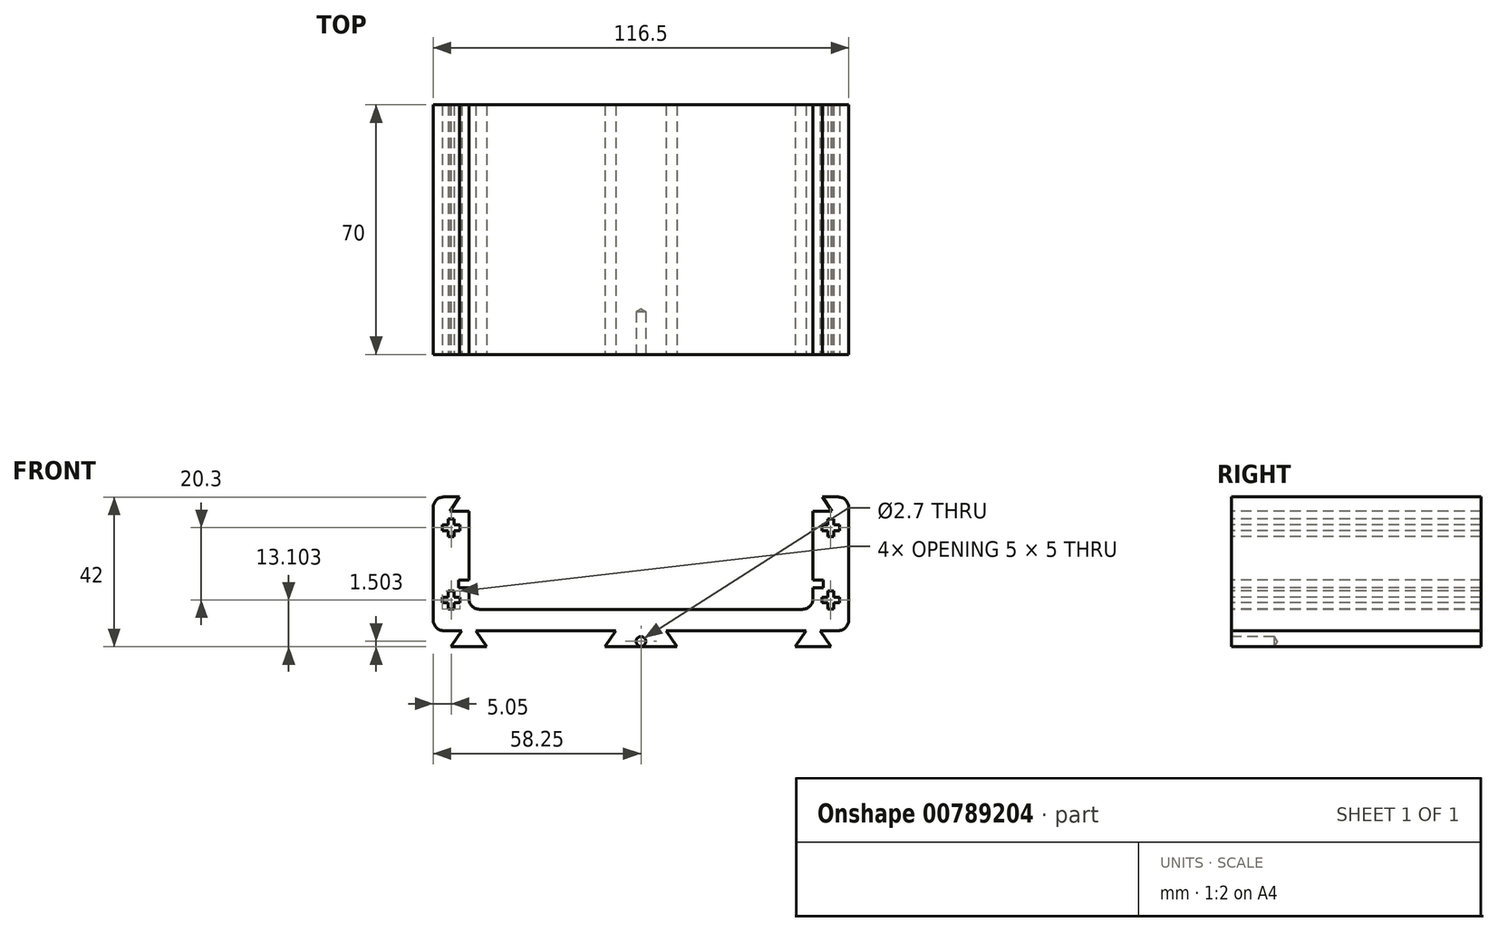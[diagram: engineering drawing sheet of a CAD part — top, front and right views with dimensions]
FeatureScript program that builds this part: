
annotation { "Feature Type Name" : "Feature", "Feature Type Description" : "" }
export const myFeature = defineFeature(function(context is Context, id is Id, definition is map)
    precondition{}
    {
        {
            var Q0;
            Q0=qCreatedBy(makeId("Front.planeOp"),FACE);
            var sketch = newSketch(context, id + "F0", { "sketchPlane" : qUnion([Q0])});
            skLineSegment(sketch, "E0", {"start": v(0, -17) * mm, "end": v(-10.04, -17) * mm});
            skLineSegment(sketch, "E1", {"start": v(-10.04, -17) * mm, "end": v(-7, -12.5) * mm});
            skLineSegment(sketch, "E2", {"start": v(-7, -12.5) * mm, "end": v(-46.25, -12.5) * mm});
            skLineSegment(sketch, "E3", {"start": v(-46.25, -12.5) * mm, "end": v(-43.21, -17) * mm});
            skLineSegment(sketch, "E4", {"start": v(-43.21, -17) * mm, "end": v(-53.29, -17) * mm});
            skLineSegment(sketch, "E5", {"start": v(-53.29, -17) * mm, "end": v(-50.25, -12.5) * mm});
            skLineSegment(sketch, "E6", {"start": v(-50.25, -12.5) * mm, "end": v(-55.25, -12.5) * mm});
            skLineSegment(sketch, "E7", {"start": v(-58.25, -9.5) * mm, "end": v(-58.25, 22) * mm});
            skLineSegment(sketch, "E8", {"start": v(-55.25, 25) * mm, "end": v(-50.87, 25) * mm});
            skLineSegment(sketch, "E9", {"start": v(-50.87, 25) * mm, "end": v(-53.5, 21) * mm});
            skLineSegment(sketch, "E10", {"start": v(-53.5, 21) * mm, "end": v(-48.25, 21) * mm});
            skLineSegment(sketch, "E11", {"start": v(-48.25, 21) * mm, "end": v(-48.25, 1.7) * mm});
            skLineSegment(sketch, "E12", {"start": v(-48.25, 1.7) * mm, "end": v(-51.1, 1.7) * mm});
            skLineSegment(sketch, "E13", {"start": v(-51.1, 1.7) * mm, "end": v(-51.1, -0.5) * mm});
            skLineSegment(sketch, "E14", {"start": v(-51.1, -0.5) * mm, "end": v(-48.25, -0.5) * mm});
            skLineSegment(sketch, "E15", {"start": v(-48.25, -0.5) * mm, "end": v(-48.25, -3.5) * mm});
            skLineSegment(sketch, "E16", {"start": v(-45.25, -6.5) * mm, "end": v(0, -6.5) * mm});
            skLineSegment(sketch, "E17", {"start": v(-48.25, 29.47) * mm, "end": v(-48.25, -26.87) * mm, "construction": true});
            skPoint(sketch, "E18.visualSharp", {"position": v(-58.25, 25) * mm});
            skArc(sketch, "E18.filletArc", {"start": v(-55.25, 25) * mm, "mid": v(-57.37, 24.11) * mm, "end": v(-58.25, 22) * mm});
            skPoint(sketch, "E19.visualSharp", {"position": v(-58.25, -12.5) * mm});
            skArc(sketch, "E19.filletArc", {"start": v(-58.25, -9.5) * mm, "mid": v(-57.37, -11.63) * mm, "end": v(-55.25, -12.5) * mm});
            skPoint(sketch, "E20.visualSharp", {"position": v(-48.25, -6.5) * mm});
            skArc(sketch, "E20.filletArc", {"start": v(-48.25, -3.5) * mm, "mid": v(-47.37, -5.63) * mm, "end": v(-45.25, -6.5) * mm});
            skLineSegment(sketch, "E21", {"start": v(-53.2, 35.2) * mm, "end": v(-53.2, -9.28) * mm, "construction": true});
            skLineSegment(sketch, "E22", {"start": v(-92.18, 6.24) * mm, "end": v(0, 6.24) * mm, "construction": true});
            skArc(sketch, "E23.MirrorCS", {"start": v(48.25, -3.5) * mm, "mid": v(47.37, -5.63) * mm, "end": v(45.25, -6.5) * mm});
            skArc(sketch, "E24.MirrorCS", {"start": v(55.25, 25) * mm, "mid": v(57.37, 24.11) * mm, "end": v(58.25, 22) * mm});
            skLineSegment(sketch, "E25.MirrorCS", {"start": v(48.25, -0.5) * mm, "end": v(48.25, -3.5) * mm});
            skLineSegment(sketch, "E26.MirrorCS", {"start": v(46.25, -12.5) * mm, "end": v(43.21, -17) * mm});
            skLineSegment(sketch, "E27.MirrorCS", {"start": v(51.1, 1.7) * mm, "end": v(51.1, -0.5) * mm});
            skLineSegment(sketch, "E28.MirrorCS", {"start": v(53.29, -17) * mm, "end": v(50.25, -12.5) * mm});
            skLineSegment(sketch, "E29.MirrorCS", {"start": v(10.04, -17) * mm, "end": v(7, -12.5) * mm});
            skLineSegment(sketch, "E30.MirrorCS", {"start": v(48.25, 1.7) * mm, "end": v(51.1, 1.7) * mm});
            skLineSegment(sketch, "E31.MirrorCS", {"start": v(51.1, -0.5) * mm, "end": v(48.25, -0.5) * mm});
            skArc(sketch, "E32.MirrorCS", {"start": v(58.25, -9.5) * mm, "mid": v(57.37, -11.63) * mm, "end": v(55.25, -12.5) * mm});
            skLineSegment(sketch, "E33.MirrorCS", {"start": v(45.25, -6.5) * mm, "end": v(0, -6.5) * mm});
            skLineSegment(sketch, "E34.MirrorCS", {"start": v(48.25, 29.47) * mm, "end": v(48.25, -26.87) * mm, "construction": true});
            skLineSegment(sketch, "E35.MirrorCS", {"start": v(0, -17) * mm, "end": v(10.04, -17) * mm});
            skPoint(sketch, "E36.MirrorP", {"position": v(58.25, -12.5) * mm});
            skLineSegment(sketch, "E37.MirrorCS", {"start": v(7, -12.5) * mm, "end": v(46.25, -12.5) * mm});
            skLineSegment(sketch, "E38.MirrorCS", {"start": v(43.21, -17) * mm, "end": v(53.29, -17) * mm});
            skPoint(sketch, "E39.MirrorP", {"position": v(58.25, 25) * mm});
            skLineSegment(sketch, "E40.MirrorCS", {"start": v(50.25, -12.5) * mm, "end": v(55.25, -12.5) * mm});
            skLineSegment(sketch, "E41.MirrorCS", {"start": v(53.2, 35.2) * mm, "end": v(53.2, -9.28) * mm, "construction": true});
            skPoint(sketch, "E42.MirrorP", {"position": v(48.25, -6.5) * mm});
            skLineSegment(sketch, "E43.MirrorCS", {"start": v(58.25, -9.5) * mm, "end": v(58.25, 22) * mm});
            skLineSegment(sketch, "E44.MirrorCS", {"start": v(53.5, 21) * mm, "end": v(48.25, 21) * mm});
            skLineSegment(sketch, "E45.MirrorCS", {"start": v(48.25, 21) * mm, "end": v(48.25, 1.7) * mm});
            skLineSegment(sketch, "E46.MirrorCS", {"start": v(55.25, 25) * mm, "end": v(50.87, 25) * mm});
            skLineSegment(sketch, "E47.MirrorCS", {"start": v(50.87, 25) * mm, "end": v(53.5, 21) * mm});
            skPoint(sketch, "E48", {"position": v(-53.2, 16.4) * mm});
            skPoint(sketch, "E49", {"position": v(-53.2, -3.9) * mm});
            skLineSegment(sketch, "E50", {"start": v(-55.7, 17.2) * mm, "end": v(-54, 17.2) * mm});
            skLineSegment(sketch, "E51", {"start": v(-54, 17.2) * mm, "end": v(-54, 18.9) * mm});
            skLineSegment(sketch, "E52", {"start": v(-54, 18.9) * mm, "end": v(-52.4, 18.9) * mm});
            skLineSegment(sketch, "E53", {"start": v(-52.4, 18.9) * mm, "end": v(-52.4, 17.2) * mm});
            skLineSegment(sketch, "E54", {"start": v(-52.4, 17.2) * mm, "end": v(-50.7, 17.2) * mm});
            skLineSegment(sketch, "E55", {"start": v(-50.7, 17.2) * mm, "end": v(-50.7, 15.6) * mm});
            skLineSegment(sketch, "E56", {"start": v(-50.7, 15.6) * mm, "end": v(-52.4, 15.6) * mm});
            skLineSegment(sketch, "E57", {"start": v(-52.4, 15.6) * mm, "end": v(-52.4, 13.9) * mm});
            skLineSegment(sketch, "E58", {"start": v(-52.4, 13.9) * mm, "end": v(-54, 13.9) * mm});
            skLineSegment(sketch, "E59", {"start": v(-54, 13.9) * mm, "end": v(-54, 15.6) * mm});
            skLineSegment(sketch, "E60", {"start": v(-54, 15.6) * mm, "end": v(-55.7, 15.6) * mm});
            skLineSegment(sketch, "E61", {"start": v(-55.7, 15.6) * mm, "end": v(-55.7, 17.2) * mm});
            skLineSegment(sketch, "E62", {"start": v(-50.4, 16.4) * mm, "end": v(-59.4, 16.4) * mm, "construction": true});
            skLineSegment(sketch, "E63", {"start": v(-49.34, -3.9) * mm, "end": v(-57.36, -3.9) * mm, "construction": true});
            skLineSegment(sketch, "E64", {"start": v(-54, -1.4) * mm, "end": v(-52.4, -1.4) * mm});
            skLineSegment(sketch, "E65", {"start": v(-52.4, -1.4) * mm, "end": v(-52.4, -3.1) * mm});
            skLineSegment(sketch, "E66", {"start": v(-52.4, -3.1) * mm, "end": v(-50.7, -3.1) * mm});
            skLineSegment(sketch, "E67", {"start": v(-50.7, -3.1) * mm, "end": v(-50.7, -4.7) * mm});
            skLineSegment(sketch, "E68", {"start": v(-50.7, -4.7) * mm, "end": v(-52.4, -4.7) * mm});
            skLineSegment(sketch, "E69", {"start": v(-52.4, -4.7) * mm, "end": v(-52.4, -6.4) * mm});
            skLineSegment(sketch, "E70", {"start": v(-52.4, -6.4) * mm, "end": v(-54, -6.4) * mm});
            skLineSegment(sketch, "E71", {"start": v(-54, -6.4) * mm, "end": v(-54, -4.7) * mm});
            skLineSegment(sketch, "E72", {"start": v(-54, -4.7) * mm, "end": v(-55.7, -4.7) * mm});
            skLineSegment(sketch, "E73", {"start": v(-55.7, -4.7) * mm, "end": v(-55.7, -3.1) * mm});
            skLineSegment(sketch, "E74", {"start": v(-55.7, -3.1) * mm, "end": v(-54, -3.1) * mm});
            skLineSegment(sketch, "E75", {"start": v(-54, -3.1) * mm, "end": v(-54, -1.4) * mm});
            skLineSegment(sketch, "E76.MirrorCS", {"start": v(54, 17.2) * mm, "end": v(54, 18.9) * mm});
            skLineSegment(sketch, "E77.MirrorCS", {"start": v(54, 18.9) * mm, "end": v(52.4, 18.9) * mm});
            skLineSegment(sketch, "E78.MirrorCS", {"start": v(52.4, 18.9) * mm, "end": v(52.4, 17.2) * mm});
            skLineSegment(sketch, "E79.MirrorCS", {"start": v(52.4, 17.2) * mm, "end": v(50.7, 17.2) * mm});
            skLineSegment(sketch, "E80.MirrorCS", {"start": v(50.7, 17.2) * mm, "end": v(50.7, 15.6) * mm});
            skLineSegment(sketch, "E81.MirrorCS", {"start": v(50.7, 15.6) * mm, "end": v(52.4, 15.6) * mm});
            skLineSegment(sketch, "E82.MirrorCS", {"start": v(52.4, 15.6) * mm, "end": v(52.4, 13.9) * mm});
            skLineSegment(sketch, "E83.MirrorCS", {"start": v(52.4, 13.9) * mm, "end": v(54, 13.9) * mm});
            skLineSegment(sketch, "E84.MirrorCS", {"start": v(54, 13.9) * mm, "end": v(54, 15.6) * mm});
            skLineSegment(sketch, "E85.MirrorCS", {"start": v(54, 15.6) * mm, "end": v(55.7, 15.6) * mm});
            skLineSegment(sketch, "E86.MirrorCS", {"start": v(55.7, 15.6) * mm, "end": v(55.7, 17.2) * mm});
            skLineSegment(sketch, "E87.MirrorCS", {"start": v(55.7, 17.2) * mm, "end": v(54, 17.2) * mm});
            skLineSegment(sketch, "E88.MirrorCS", {"start": v(54, -1.4) * mm, "end": v(52.4, -1.4) * mm});
            skLineSegment(sketch, "E89.MirrorCS", {"start": v(52.4, -1.4) * mm, "end": v(52.4, -3.1) * mm});
            skLineSegment(sketch, "E90.MirrorCS", {"start": v(52.4, -3.1) * mm, "end": v(50.7, -3.1) * mm});
            skLineSegment(sketch, "E91.MirrorCS", {"start": v(50.7, -3.1) * mm, "end": v(50.7, -4.7) * mm});
            skLineSegment(sketch, "E92.MirrorCS", {"start": v(50.7, -4.7) * mm, "end": v(52.4, -4.7) * mm});
            skLineSegment(sketch, "E93.MirrorCS", {"start": v(52.4, -4.7) * mm, "end": v(52.4, -6.4) * mm});
            skLineSegment(sketch, "E94.MirrorCS", {"start": v(52.4, -6.4) * mm, "end": v(54, -6.4) * mm});
            skLineSegment(sketch, "E95.MirrorCS", {"start": v(54, -6.4) * mm, "end": v(54, -4.7) * mm});
            skLineSegment(sketch, "E96.MirrorCS", {"start": v(54, -4.7) * mm, "end": v(55.7, -4.7) * mm});
            skLineSegment(sketch, "E97.MirrorCS", {"start": v(55.7, -4.7) * mm, "end": v(55.7, -3.1) * mm});
            skLineSegment(sketch, "E98.MirrorCS", {"start": v(55.7, -3.1) * mm, "end": v(54, -3.1) * mm});
            skLineSegment(sketch, "E99.MirrorCS", {"start": v(54, -3.1) * mm, "end": v(54, -1.4) * mm});
            skSolve(sketch);
        }
        {
            var Q0;
            Q0=qSketchRegion(id+"F0",true);
            extrude(context, id + "F1", {"entities" : qUnion([Q0]), "oppositeDirection" : true, "depth" : 70 * mm});
        }
        {
            var Q0;
            Q0=makeQuery(id+"F1.opExtrude","CAP_FACE",FACE,{"disambiguationData":[OSD([sQuery(id+"F0.wireOp",EDGE,"E0"),sQuery(id+"F0.wireOp",EDGE,"E1"),sQuery(id+"F0.wireOp",EDGE,"E2"),sQuery(id+"F0.wireOp",EDGE,"E3"),sQuery(id+"F0.wireOp",EDGE,"E4"),sQuery(id+"F0.wireOp",EDGE,"E5"),sQuery(id+"F0.wireOp",EDGE,"E6"),sQuery(id+"F0.wireOp",EDGE,"E7"),sQuery(id+"F0.wireOp",EDGE,"E8"),sQuery(id+"F0.wireOp",EDGE,"E9"),sQuery(id+"F0.wireOp",EDGE,"E10"),sQuery(id+"F0.wireOp",EDGE,"E11"),sQuery(id+"F0.wireOp",EDGE,"E12"),sQuery(id+"F0.wireOp",EDGE,"E13"),sQuery(id+"F0.wireOp",EDGE,"E14"),sQuery(id+"F0.wireOp",EDGE,"E15"),sQuery(id+"F0.wireOp",EDGE,"E16"),sQuery(id+"F0.wireOp",EDGE,"E18.filletArc"),sQuery(id+"F0.wireOp",EDGE,"E19.filletArc"),sQuery(id+"F0.wireOp",EDGE,"E20.filletArc"),sQuery(id+"F0.wireOp",EDGE,"5194898a-ef6c-4157-a49c-2c8236cce61c"),sQuery(id+"F0.wireOp",EDGE,"7f281998-eedb-455a-a055-9dc59b9fbc9e"),sQuery(id+"F0.wireOp",EDGE,"E23.MirrorCS"),sQuery(id+"F0.wireOp",EDGE,"E24.MirrorCS"),sQuery(id+"F0.wireOp",EDGE,"E25.MirrorCS"),sQuery(id+"F0.wireOp",EDGE,"E26.MirrorCS"),sQuery(id+"F0.wireOp",EDGE,"E27.MirrorCS"),sQuery(id+"F0.wireOp",EDGE,"E28.MirrorCS"),sQuery(id+"F0.wireOp",EDGE,"E29.MirrorCS"),sQuery(id+"F0.wireOp",EDGE,"E30.MirrorCS"),sQuery(id+"F0.wireOp",EDGE,"E31.MirrorCS"),sQuery(id+"F0.wireOp",EDGE,"d584a0aa-b8c3-4ab9-8824-3ea712040d109.MirrorC"),sQuery(id+"F0.wireOp",EDGE,"E32.MirrorCS"),sQuery(id+"F0.wireOp",EDGE,"E241.MirrorC"),sQuery(id+"F0.wireOp",EDGE,"E33.MirrorCS"),sQuery(id+"F0.wireOp",EDGE,"E35.MirrorCS"),sQuery(id+"F0.wireOp",EDGE,"E37.MirrorCS"),sQuery(id+"F0.wireOp",EDGE,"E38.MirrorCS"),sQuery(id+"F0.wireOp",EDGE,"E40.MirrorCS"),sQuery(id+"F0.wireOp",EDGE,"E43.MirrorCS"),sQuery(id+"F0.wireOp",EDGE,"E44.MirrorCS"),sQuery(id+"F0.wireOp",EDGE,"E45.MirrorCS"),sQuery(id+"F0.wireOp",EDGE,"E46.MirrorCS"),sQuery(id+"F0.wireOp",EDGE,"E47.MirrorCS")])],"isStart":true});
            var sketch = newSketch(context, id + "F2", { "sketchPlane" : qUnion([Q0])});
            skPoint(sketch, "E100", {"position": v(0, -15.5) * mm});
            skSolve(sketch);
        }
        {
            var Q0;
            Q0=sQuery(id+"F2.wireOp",VERTEX,"E100");
            var Q1;
            Q1=makeQuery(id+"F1.opExtrude","SWEPT_BODY",BODY,{"disambiguationData":[OSD([sQuery(id+"F0.wireOp",EDGE,"E0"),sQuery(id+"F0.wireOp",EDGE,"E1"),sQuery(id+"F0.wireOp",EDGE,"E2"),sQuery(id+"F0.wireOp",EDGE,"E3"),sQuery(id+"F0.wireOp",EDGE,"E4"),sQuery(id+"F0.wireOp",EDGE,"E5"),sQuery(id+"F0.wireOp",EDGE,"E6"),sQuery(id+"F0.wireOp",EDGE,"E7"),sQuery(id+"F0.wireOp",EDGE,"E8"),sQuery(id+"F0.wireOp",EDGE,"E9"),sQuery(id+"F0.wireOp",EDGE,"E10"),sQuery(id+"F0.wireOp",EDGE,"E11"),sQuery(id+"F0.wireOp",EDGE,"E12"),sQuery(id+"F0.wireOp",EDGE,"E13"),sQuery(id+"F0.wireOp",EDGE,"E14"),sQuery(id+"F0.wireOp",EDGE,"E15"),sQuery(id+"F0.wireOp",EDGE,"E16"),sQuery(id+"F0.wireOp",EDGE,"E18.filletArc"),sQuery(id+"F0.wireOp",EDGE,"E19.filletArc"),sQuery(id+"F0.wireOp",EDGE,"E20.filletArc"),sQuery(id+"F0.wireOp",EDGE,"5194898a-ef6c-4157-a49c-2c8236cce61c"),sQuery(id+"F0.wireOp",EDGE,"7f281998-eedb-455a-a055-9dc59b9fbc9e"),sQuery(id+"F0.wireOp",EDGE,"E23.MirrorCS"),sQuery(id+"F0.wireOp",EDGE,"E24.MirrorCS"),sQuery(id+"F0.wireOp",EDGE,"E25.MirrorCS"),sQuery(id+"F0.wireOp",EDGE,"E26.MirrorCS"),sQuery(id+"F0.wireOp",EDGE,"E27.MirrorCS"),sQuery(id+"F0.wireOp",EDGE,"E28.MirrorCS"),sQuery(id+"F0.wireOp",EDGE,"E29.MirrorCS"),sQuery(id+"F0.wireOp",EDGE,"E30.MirrorCS"),sQuery(id+"F0.wireOp",EDGE,"E31.MirrorCS"),sQuery(id+"F0.wireOp",EDGE,"d584a0aa-b8c3-4ab9-8824-3ea712040d109.MirrorC"),sQuery(id+"F0.wireOp",EDGE,"E32.MirrorCS"),sQuery(id+"F0.wireOp",EDGE,"E241.MirrorC"),sQuery(id+"F0.wireOp",EDGE,"E33.MirrorCS"),sQuery(id+"F0.wireOp",EDGE,"E35.MirrorCS"),sQuery(id+"F0.wireOp",EDGE,"E37.MirrorCS"),sQuery(id+"F0.wireOp",EDGE,"E38.MirrorCS"),sQuery(id+"F0.wireOp",EDGE,"E40.MirrorCS"),sQuery(id+"F0.wireOp",EDGE,"E43.MirrorCS"),sQuery(id+"F0.wireOp",EDGE,"E44.MirrorCS"),sQuery(id+"F0.wireOp",EDGE,"E45.MirrorCS"),sQuery(id+"F0.wireOp",EDGE,"E46.MirrorCS"),sQuery(id+"F0.wireOp",EDGE,"E47.MirrorCS")])]});
            hole(context, id + "F3", {"style" : HoleStyle.SIMPLE, "holeDiameter" : 2.7 * mm, "endStyle" : HoleEndStyle.BLIND, "holeDepth" : 12 * mm, "locations" : qUnion([Q0]), "scope" : qUnion([Q1])});
        }
    });
